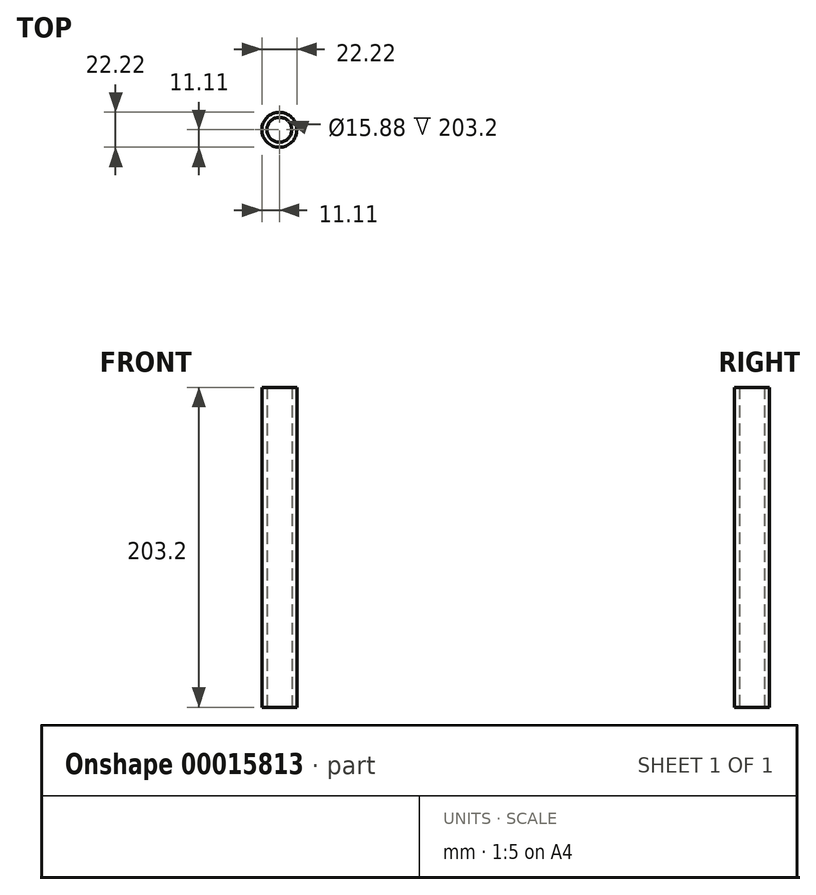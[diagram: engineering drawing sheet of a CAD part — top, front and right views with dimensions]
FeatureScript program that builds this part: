
annotation { "Feature Type Name" : "Feature", "Feature Type Description" : "" }
export const myFeature = defineFeature(function(context is Context, id is Id, definition is map)
    precondition{}
    {
        {
            var Q0;
            Q0=qCreatedBy(makeId("Top.planeOp"),FACE);
            var sketch = newSketch(context, id + "F0", { "sketchPlane" : qUnion([Q0])});
            skCircle(sketch, "E0", {"center": v(0, 0) * mm, "radius": 7.94 * mm});
            skCircle(sketch, "E1", {"center": v(0, 0) * mm, "radius": 11.11 * mm});
            skSolve(sketch);
        }
        {
            var Q0;
            Q0=qSketchRegion(id+"F0",true);
            extrude(context, id + "F1", {"entities" : qUnion([Q0]), "depth" : 203.2 * mm});
        }
    });
